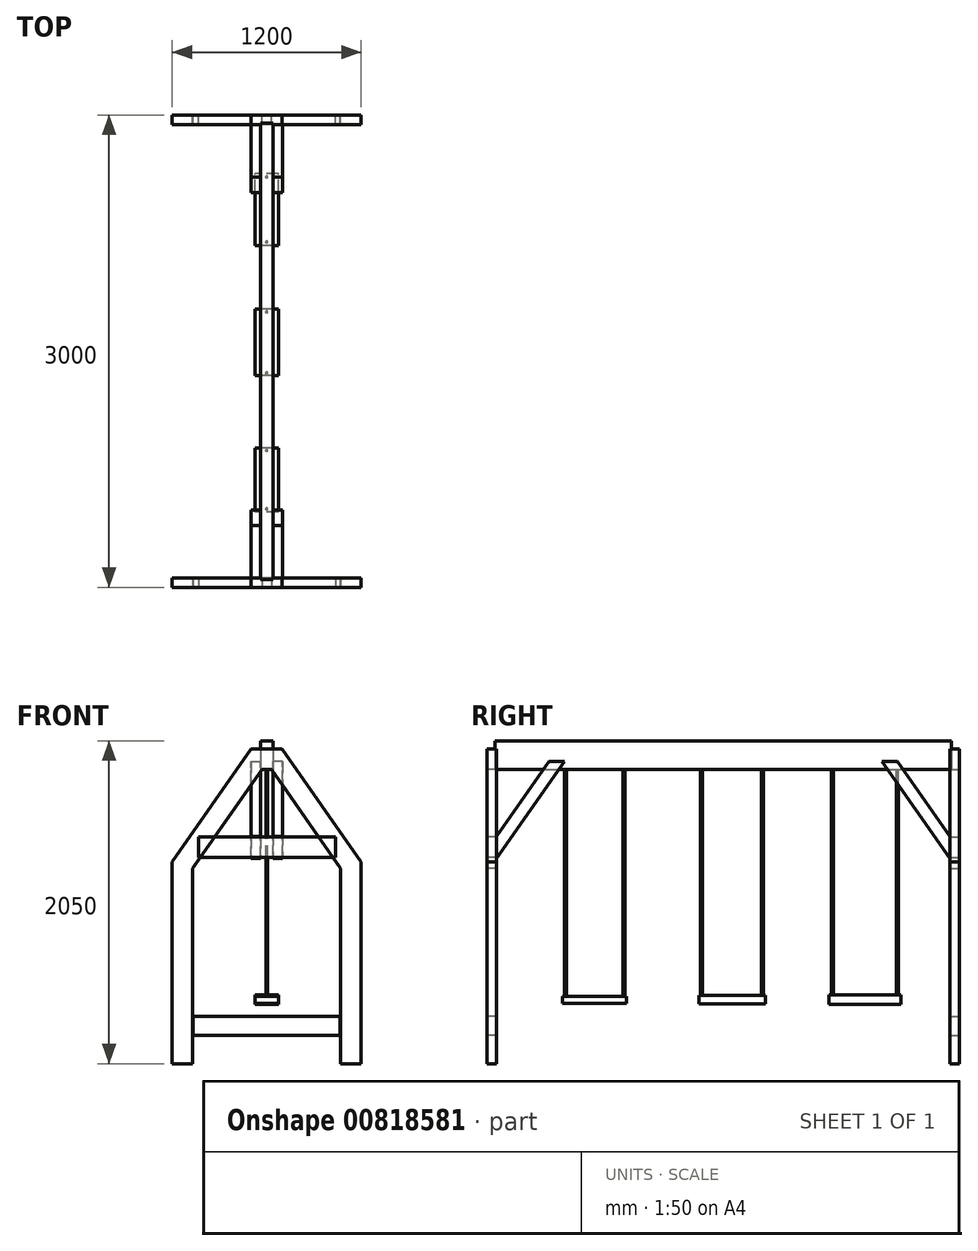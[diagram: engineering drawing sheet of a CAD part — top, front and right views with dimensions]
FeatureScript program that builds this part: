
annotation { "Feature Type Name" : "Feature", "Feature Type Description" : "" }
export const myFeature = defineFeature(function(context is Context, id is Id, definition is map)
    precondition{}
    {
        {
            var Q0;
            Q0=qCreatedBy(makeId("Front.planeOp"),FACE);
            var sketch = newSketch(context, id + "F0", { "sketchPlane" : qUnion([Q0])});
            skLineSegment(sketch, "E0", {"start": v(-97.67, 2000) * mm, "end": v(0, 2000) * mm});
            skLineSegment(sketch, "E1", {"start": v(-97.67, 2000) * mm, "end": v(-600, 1282.6) * mm});
            skLineSegment(sketch, "E2", {"start": v(-600, 1282.6) * mm, "end": v(-600, 0) * mm});
            skLineSegment(sketch, "E3", {"start": v(0, 2000) * mm, "end": v(0, 0) * mm, "construction": true});
            skLineSegment(sketch, "E4.MirrorCS", {"start": v(600, 1282.6) * mm, "end": v(600, 0) * mm});
            skLineSegment(sketch, "E5.MirrorCS", {"start": v(97.67, 2000) * mm, "end": v(0, 2000) * mm});
            skLineSegment(sketch, "E6.MirrorCS", {"start": v(97.67, 2000) * mm, "end": v(600, 1282.6) * mm});
            skLineSegment(sketch, "E7", {"start": v(0, 1870) * mm, "end": v(-30, 1870) * mm});
            skLineSegment(sketch, "E8", {"start": v(-30, 1870) * mm, "end": v(-470, 1241.61) * mm});
            skLineSegment(sketch, "E9", {"start": v(-470, 1241.61) * mm, "end": v(-470, 0) * mm});
            skLineSegment(sketch, "E10", {"start": v(-470, 0) * mm, "end": v(-600, 0) * mm});
            skLineSegment(sketch, "E11", {"start": v(-576.49, 1316.18) * mm, "end": v(-470, 1241.61) * mm, "construction": true});
            skLineSegment(sketch, "E12", {"start": v(-30, 2000) * mm, "end": v(-30, 1870) * mm, "construction": true});
            skLineSegment(sketch, "E13.MirrorCS", {"start": v(470, 0) * mm, "end": v(600, 0) * mm});
            skLineSegment(sketch, "E14.MirrorCS", {"start": v(470, 1241.61) * mm, "end": v(470, 0) * mm});
            skLineSegment(sketch, "E15.MirrorCS", {"start": v(0, 1870) * mm, "end": v(30, 1870) * mm});
            skLineSegment(sketch, "E16.MirrorCS", {"start": v(30, 1870) * mm, "end": v(470, 1241.61) * mm});
            skSolve(sketch);
        }
        {
            var Q0;
            Q0=makeQuery(id+"F0.imprint","IMPRINT",FACE,{"disambiguationData":[TD([[makeQuery(id+"F0.imprint","IMPRINT",EDGE,{"derivedFrom":sQuery(id+"F0.wireOp",EDGE,"E0")}),-1.0]])]});
            extrude(context, id + "F1", {"entities" : qUnion([Q0]), "depth" : 60 * mm, "offsetDistance" : 25 * mm});
        }
        {
            var Q0;
            Q0=qCreatedBy(makeId("Front.planeOp"),FACE);
            cPlane(context, id + "F2", {"entities" : qUnion([Q0]), "cplaneType" : CPlaneType.OFFSET, "offset" : 3000 * mm, "width" : 150 * mm, "height" : 150 * mm});
        }
        {
            var Q0;
            Q0=qCreatedBy(id+"F2.planeOp",FACE);
            var sketch = newSketch(context, id + "F3", { "sketchPlane" : qUnion([Q0])});
            skLineSegment(sketch, "E17.0.0", {"start": v(-30, 1870) * mm, "end": v(30, 1870) * mm});
            skLineSegment(sketch, "E17.0.1", {"start": v(30, 1870) * mm, "end": v(470, 1241.61) * mm});
            skLineSegment(sketch, "E17.0.2", {"start": v(470, 1241.61) * mm, "end": v(470, 0) * mm});
            skLineSegment(sketch, "E17.0.3", {"start": v(470, 0) * mm, "end": v(600, 0) * mm});
            skLineSegment(sketch, "E17.0.4", {"start": v(600, 0) * mm, "end": v(600, 1282.6) * mm});
            skLineSegment(sketch, "E17.0.5", {"start": v(600, 1282.6) * mm, "end": v(97.67, 2000) * mm});
            skLineSegment(sketch, "E17.0.6", {"start": v(97.67, 2000) * mm, "end": v(-97.67, 2000) * mm});
            skLineSegment(sketch, "E17.0.7", {"start": v(-97.67, 2000) * mm, "end": v(-600, 1282.6) * mm});
            skLineSegment(sketch, "E17.0.8", {"start": v(-600, 1282.6) * mm, "end": v(-600, 0) * mm});
            skLineSegment(sketch, "E17.0.9", {"start": v(-600, 0) * mm, "end": v(-470, 0) * mm});
            skLineSegment(sketch, "E17.0.10", {"start": v(-470, 0) * mm, "end": v(-470, 1241.61) * mm});
            skLineSegment(sketch, "E17.0.11", {"start": v(-470, 1241.61) * mm, "end": v(-30, 1870) * mm});
            skSolve(sketch);
        }
        {
            var Q0;
            Q0=makeQuery(id+"F3.imprint","IMPRINT",FACE,{"disambiguationData":[TD([[makeQuery(id+"F3.imprint","IMPRINT",EDGE,{"derivedFrom":sQuery(id+"F3.wireOp",EDGE,"E17.0.0")}),1.0]])]});
            extrude(context, id + "F4", {"entities" : qUnion([Q0]), "oppositeDirection" : true, "depth" : 60 * mm, "offsetDistance" : 25 * mm});
        }
        {
            var Q0;
            Q0=qCreatedBy(makeId("Front.planeOp"),FACE);
            var sketch = newSketch(context, id + "F5", { "sketchPlane" : qUnion([Q0])});
            skLineSegment(sketch, "E18.bottom", {"start": v(-39.63, 2050) * mm, "end": v(40.37, 2050) * mm});
            skLineSegment(sketch, "E18.top", {"start": v(-39.63, 1870) * mm, "end": v(40.37, 1870) * mm});
            skLineSegment(sketch, "E18.left", {"start": v(-39.63, 2050) * mm, "end": v(-39.63, 1870) * mm});
            skLineSegment(sketch, "E18.right", {"start": v(40.37, 2050) * mm, "end": v(40.37, 1870) * mm});
            skSolve(sketch);
        }
        {
            var Q0;
            Q0=qSketchRegion(id+"F5",true);
            extrude(context, id + "F6", {"entities" : qUnion([Q0]), "depth" : 2950 * mm, "offsetDistance" : 25 * mm, "hasSecondDirection" : true, "secondDirectionOppositeDirection" : false, "secondDirectionDepth" : 50 * mm});
        }
        {
            var Q0;
            Q0=qCreatedBy(id+"F2.planeOp",FACE);
            var sketch = newSketch(context, id + "F7", { "sketchPlane" : qUnion([Q0])});
            skLineSegment(sketch, "E19.bottom", {"start": v(-432.67, 1311) * mm, "end": v(438, 1311) * mm});
            skLineSegment(sketch, "E19.top", {"start": v(-432.67, 1441.47) * mm, "end": v(438, 1441.47) * mm});
            skLineSegment(sketch, "E19.left", {"start": v(-432.67, 1441.47) * mm, "end": v(-432.67, 1311) * mm});
            skLineSegment(sketch, "E19.right", {"start": v(438, 1441.47) * mm, "end": v(438, 1311) * mm});
            skLineSegment(sketch, "E20.bottom", {"start": v(-467.28, 299.22) * mm, "end": v(467.28, 299.22) * mm});
            skLineSegment(sketch, "E20.top", {"start": v(-467.28, 179.4) * mm, "end": v(467.28, 179.4) * mm});
            skLineSegment(sketch, "E20.left", {"start": v(-467.28, 299.22) * mm, "end": v(-467.28, 179.4) * mm});
            skLineSegment(sketch, "E20.right", {"start": v(467.28, 299.22) * mm, "end": v(467.28, 179.4) * mm});
            skSolve(sketch);
        }
        {
            var Q0;
            Q0=qSketchRegion(id+"F7",true);
            extrude(context, id + "F8", {"entities" : qUnion([Q0]), "oppositeDirection" : true, "depth" : 60 * mm, "offsetDistance" : 25 * mm});
        }
        {
            var Q0;
            Q0=qCreatedBy(makeId("Front.planeOp"),FACE);
            var sketch = newSketch(context, id + "F9", { "sketchPlane" : qUnion([Q0])});
            skLineSegment(sketch, "E21.0.0", {"start": v(-432.67, 1441.47) * mm, "end": v(-432.67, 1311) * mm});
            skLineSegment(sketch, "E21.0.1", {"start": v(438, 1441.47) * mm, "end": v(-432.67, 1441.47) * mm});
            skLineSegment(sketch, "E21.0.2", {"start": v(438, 1311) * mm, "end": v(438, 1441.47) * mm});
            skLineSegment(sketch, "E21.0.3", {"start": v(-432.67, 1311) * mm, "end": v(438, 1311) * mm});
            skLineSegment(sketch, "E22.0.0", {"start": v(-467.28, 299.22) * mm, "end": v(-467.28, 179.4) * mm});
            skLineSegment(sketch, "E22.0.1", {"start": v(-467.28, 179.4) * mm, "end": v(467.28, 179.4) * mm});
            skLineSegment(sketch, "E22.0.2", {"start": v(467.28, 179.4) * mm, "end": v(467.28, 299.22) * mm});
            skLineSegment(sketch, "E22.0.3", {"start": v(467.28, 299.22) * mm, "end": v(-467.28, 299.22) * mm});
            skSolve(sketch);
        }
        {
            var Q0;
            Q0=qSketchRegion(id+"F9",true);
            extrude(context, id + "F10", {"entities" : qUnion([Q0]), "depth" : 60 * mm, "offsetDistance" : 25 * mm});
        }
        {
            var Q0;
            Q0=makeQuery(id+"F6.opExtrude","SWEPT_FACE",FACE,{"disambiguationData":[OSD([sQuery(id+"F5.wireOp",EDGE,"E18.right")])]});
            var sketch = newSketch(context, id + "F11", { "sketchPlane" : qUnion([Q0])});
            skLineSegment(sketch, "E23", {"start": v(-2940, 1443.65) * mm, "end": v(-2605.66, 1921.14) * mm});
            skLineSegment(sketch, "E24", {"start": v(-2605.66, 1921.14) * mm, "end": v(-2508, 1921.14) * mm});
            skLineSegment(sketch, "E25", {"start": v(-2508, 1921.14) * mm, "end": v(-2940, 1304.18) * mm});
            skLineSegment(sketch, "E26", {"start": v(-2940, 1304.18) * mm, "end": v(-2940, 1443.65) * mm});
            skLineSegment(sketch, "E27", {"start": v(-1500, 1870) * mm, "end": v(-1500, 1158.19) * mm, "construction": true});
            skLineSegment(sketch, "E28.MirrorCS", {"start": v(-492, 1921.14) * mm, "end": v(-60, 1304.18) * mm});
            skLineSegment(sketch, "E29.MirrorCS", {"start": v(-394.34, 1921.14) * mm, "end": v(-492, 1921.14) * mm});
            skLineSegment(sketch, "E30.MirrorCS", {"start": v(-60, 1443.65) * mm, "end": v(-394.34, 1921.14) * mm});
            skLineSegment(sketch, "E31.MirrorCS", {"start": v(-60, 1304.18) * mm, "end": v(-60, 1443.65) * mm});
            skSolve(sketch);
        }
        {
            var Q0;
            Q0=qSketchRegion(id+"F11",true);
            extrude(context, id + "F12", {"entities" : qUnion([Q0]), "depth" : 60 * mm, "offsetDistance" : 25 * mm});
        }
        {
            var Q0;
            Q0=makeQuery(id+"F6.opExtrude","SWEPT_FACE",FACE,{"disambiguationData":[OSD([sQuery(id+"F5.wireOp",EDGE,"E18.left")])]});
            var sketch = newSketch(context, id + "F13", { "sketchPlane" : qUnion([Q0])});
            skLineSegment(sketch, "E32.0.0", {"start": v(2940, 1304.18) * mm, "end": v(2508, 1921.14) * mm});
            skLineSegment(sketch, "E32.0.1", {"start": v(2508, 1921.14) * mm, "end": v(2605.66, 1921.14) * mm});
            skLineSegment(sketch, "E32.0.2", {"start": v(2605.66, 1921.14) * mm, "end": v(2940, 1443.65) * mm});
            skLineSegment(sketch, "E32.0.3", {"start": v(2940, 1443.65) * mm, "end": v(2940, 1304.18) * mm});
            skLineSegment(sketch, "E33.0.0", {"start": v(60, 1304.18) * mm, "end": v(60, 1443.65) * mm});
            skLineSegment(sketch, "E33.0.1", {"start": v(60, 1443.65) * mm, "end": v(394.34, 1921.14) * mm});
            skLineSegment(sketch, "E33.0.2", {"start": v(394.34, 1921.14) * mm, "end": v(492, 1921.14) * mm});
            skLineSegment(sketch, "E33.0.3", {"start": v(492, 1921.14) * mm, "end": v(60, 1304.18) * mm});
            skSolve(sketch);
        }
        {
            var Q0;
            Q0 = qSketchRegion(id + "F13", true);
            extrude(context, id + "F14", {"entities" : qUnion([Q0]), "depth" : 60 * mm, "offsetDistance" : 25 * mm});
        }
        {
            var Q0;
            Q0=qCreatedBy(makeId("Right.planeOp"),FACE);
            var sketch = newSketch(context, id + "F15", { "sketchPlane" : qUnion([Q0])});
            skLineSegment(sketch, "E34.bottom", {"start": v(-2521.04, 427.02) * mm, "end": v(-2113.58, 427.02) * mm});
            skLineSegment(sketch, "E34.top", {"start": v(-2521.04, 384.42) * mm, "end": v(-2113.58, 384.42) * mm});
            skLineSegment(sketch, "E34.left", {"start": v(-2521.04, 427.02) * mm, "end": v(-2521.04, 384.42) * mm});
            skLineSegment(sketch, "E34.right", {"start": v(-2113.58, 427.02) * mm, "end": v(-2113.58, 384.42) * mm});
            skLineSegment(sketch, "E35.bottom", {"start": v(-1652.88, 432.35) * mm, "end": v(-1232.19, 432.35) * mm});
            skLineSegment(sketch, "E35.top", {"start": v(-1652.88, 379.1) * mm, "end": v(-1232.19, 379.1) * mm});
            skLineSegment(sketch, "E35.left", {"start": v(-1652.88, 432.35) * mm, "end": v(-1652.88, 379.1) * mm});
            skLineSegment(sketch, "E35.right", {"start": v(-1232.19, 432.35) * mm, "end": v(-1232.19, 379.1) * mm});
            skLineSegment(sketch, "E36.bottom", {"start": v(-830.13, 437.68) * mm, "end": v(-372.17, 437.68) * mm});
            skLineSegment(sketch, "E36.top", {"start": v(-830.13, 376.44) * mm, "end": v(-372.17, 376.44) * mm});
            skLineSegment(sketch, "E36.left", {"start": v(-830.13, 437.68) * mm, "end": v(-830.13, 376.44) * mm});
            skLineSegment(sketch, "E36.right", {"start": v(-372.17, 437.68) * mm, "end": v(-372.17, 376.44) * mm});
            skSolve(sketch);
        }
        {
            var Q0;
            Q0 = qSketchRegion(id + "F15", true);
            extrude(context, id + "F16", {"entities" : qUnion([Q0]), "endBound" : BoundingType.SYMMETRIC, "depth" : 150 * mm, "offsetDistance" : 25 * mm});
        }
        {
            var Q0;
            Q0=qCreatedBy(makeId("Right.planeOp"),FACE);
            var sketch = newSketch(context, id + "F17", { "sketchPlane" : qUnion([Q0])});
            skLineSegment(sketch, "E37.bottom", {"start": v(-2507.57, 432.35) * mm, "end": v(-2494.25, 432.35) * mm});
            skLineSegment(sketch, "E37.top", {"start": v(-2507.57, 1864.82) * mm, "end": v(-2494.25, 1864.82) * mm});
            skLineSegment(sketch, "E37.left", {"start": v(-2507.57, 432.35) * mm, "end": v(-2507.57, 1864.82) * mm});
            skLineSegment(sketch, "E37.right", {"start": v(-2494.25, 432.35) * mm, "end": v(-2494.25, 1864.82) * mm});
            skLineSegment(sketch, "E38.bottom", {"start": v(-2137.47, 432.35) * mm, "end": v(-2124.15, 432.35) * mm});
            skLineSegment(sketch, "E38.top", {"start": v(-2137.47, 1862.16) * mm, "end": v(-2124.15, 1862.16) * mm});
            skLineSegment(sketch, "E38.left", {"start": v(-2137.47, 432.35) * mm, "end": v(-2137.47, 1862.16) * mm});
            skLineSegment(sketch, "E38.right", {"start": v(-2124.15, 432.35) * mm, "end": v(-2124.15, 1862.16) * mm});
            skLineSegment(sketch, "E39.bottom", {"start": v(-1644.89, 435.01) * mm, "end": v(-1631.57, 435.01) * mm});
            skLineSegment(sketch, "E39.top", {"start": v(-1644.89, 1867.49) * mm, "end": v(-1631.57, 1867.49) * mm});
            skLineSegment(sketch, "E39.left", {"start": v(-1644.89, 435.01) * mm, "end": v(-1644.89, 1867.49) * mm});
            skLineSegment(sketch, "E39.right", {"start": v(-1631.57, 435.01) * mm, "end": v(-1631.57, 1867.49) * mm});
            skLineSegment(sketch, "E40.bottom", {"start": v(-1258.81, 437.68) * mm, "end": v(-1245.5, 437.68) * mm});
            skLineSegment(sketch, "E40.top", {"start": v(-1258.81, 1867.49) * mm, "end": v(-1245.5, 1867.49) * mm});
            skLineSegment(sketch, "E40.left", {"start": v(-1258.81, 437.68) * mm, "end": v(-1258.81, 1867.49) * mm});
            skLineSegment(sketch, "E40.right", {"start": v(-1245.5, 437.68) * mm, "end": v(-1245.5, 1867.49) * mm});
            skLineSegment(sketch, "E41.bottom", {"start": v(-814.16, 440.34) * mm, "end": v(-800.85, 440.34) * mm});
            skLineSegment(sketch, "E41.top", {"start": v(-814.16, 1867.49) * mm, "end": v(-800.85, 1867.49) * mm});
            skLineSegment(sketch, "E41.left", {"start": v(-814.16, 440.34) * mm, "end": v(-814.16, 1867.49) * mm});
            skLineSegment(sketch, "E41.right", {"start": v(-800.85, 440.34) * mm, "end": v(-800.85, 1867.49) * mm});
            skLineSegment(sketch, "E42.bottom", {"start": v(-401.46, 440.34) * mm, "end": v(-388.15, 440.34) * mm});
            skLineSegment(sketch, "E42.top", {"start": v(-401.46, 1867.49) * mm, "end": v(-388.15, 1867.49) * mm});
            skLineSegment(sketch, "E42.left", {"start": v(-401.46, 440.34) * mm, "end": v(-401.46, 1867.49) * mm});
            skLineSegment(sketch, "E42.right", {"start": v(-388.15, 440.34) * mm, "end": v(-388.15, 1867.49) * mm});
            skSolve(sketch);
        }
        {
            var Q0;
            Q0 = qSketchRegion(id + "F17", true);
            extrude(context, id + "F18", {"entities" : qUnion([Q0]), "endBound" : BoundingType.SYMMETRIC, "depth" : 10 * mm, "offsetDistance" : 25 * mm});
        }
    });
